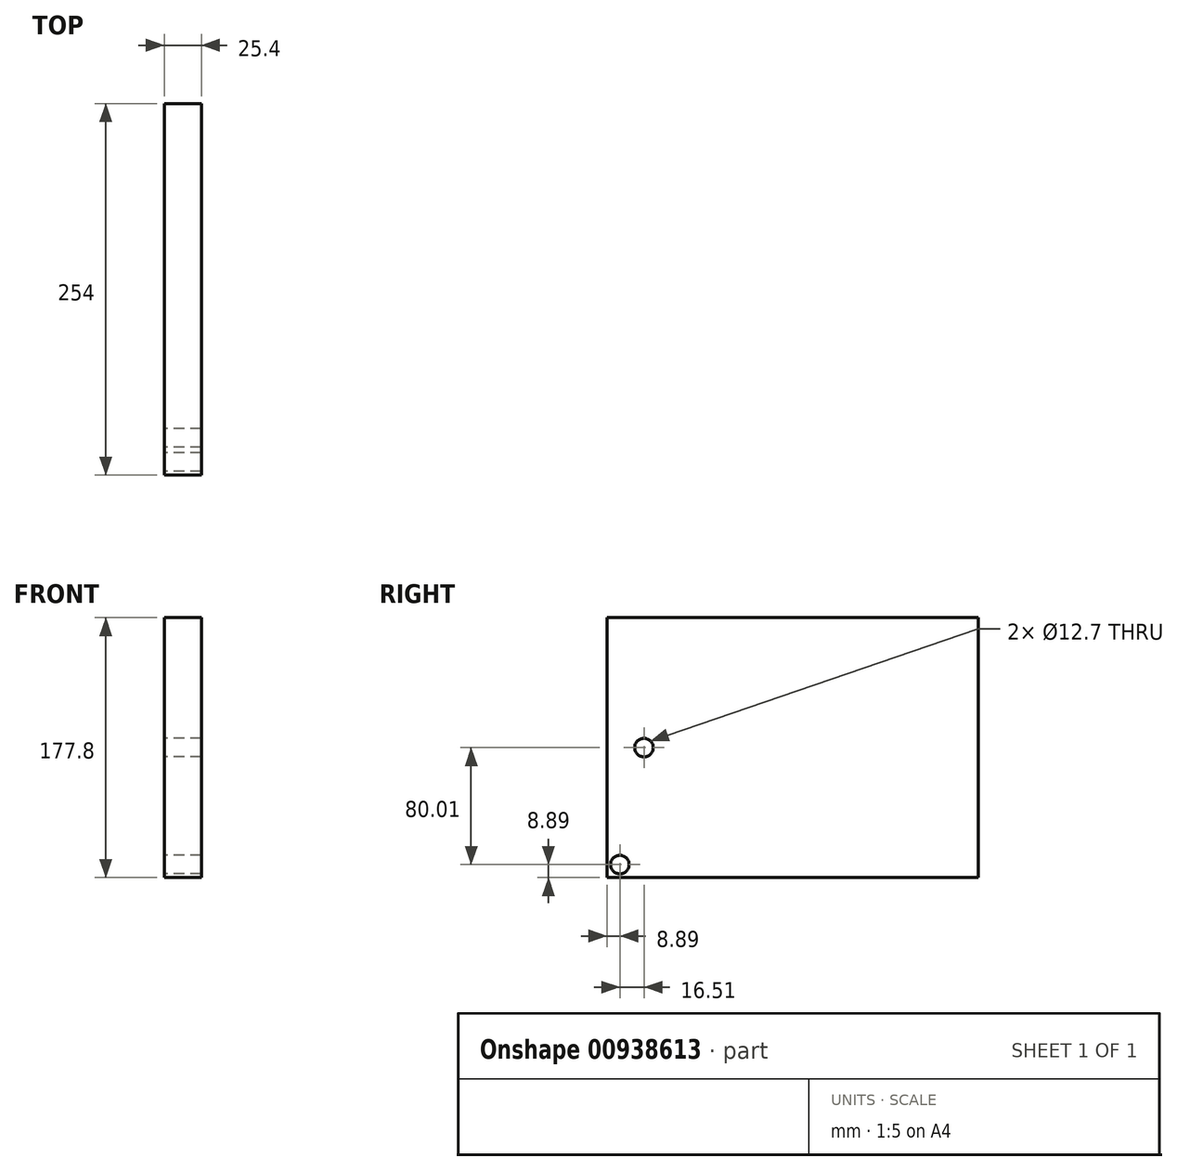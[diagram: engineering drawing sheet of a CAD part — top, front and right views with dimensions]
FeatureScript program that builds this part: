
annotation { "Feature Type Name" : "Feature", "Feature Type Description" : "" }
export const myFeature = defineFeature(function(context is Context, id is Id, definition is map)
    precondition{}
    {
        {
            var Q0;
            Q0=qCreatedBy(makeId("Right.planeOp"),FACE);
            var sketch = newSketch(context, id + "F0", { "sketchPlane" : qUnion([Q0])});
            skLineSegment(sketch, "E0.bottom", {"start": v(-127, 88.9) * mm, "end": v(127, 88.9) * mm});
            skLineSegment(sketch, "E0.top", {"start": v(-127, -88.9) * mm, "end": v(127, -88.9) * mm});
            skLineSegment(sketch, "E0.left", {"start": v(-127, 88.9) * mm, "end": v(-127, -88.9) * mm});
            skLineSegment(sketch, "E0.right", {"start": v(127, 88.9) * mm, "end": v(127, -88.9) * mm});
            skPoint(sketch, "E0.middle", {"position": v(0, 0) * mm});
            skCircle(sketch, "E1", {"center": v(-101.6, 0) * mm, "radius": 6.35 * mm});
            skCircle(sketch, "E2", {"center": v(-118.11, -80) * mm, "radius": 6.35 * mm});
            skSolve(sketch);
        }
        {
            var Q0;
            Q0=makeQuery(id+"F0.imprint","IMPRINT",FACE,{"disambiguationData":[TD([[makeQuery(id+"F0.imprint","IMPRINT",EDGE,{"derivedFrom":sQuery(id+"F0.wireOp",EDGE,"E0.bottom")}),-1.0]])]});
            extrude(context, id + "F1", {"entities" : qUnion([Q0]), "depth" : 25.4 * mm, "offsetDistance" : 25.4 * mm});
        }
    });
